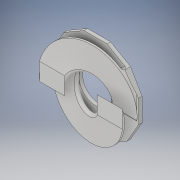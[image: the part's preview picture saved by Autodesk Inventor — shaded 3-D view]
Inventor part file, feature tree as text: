
AUTODESK INVENTOR PART (.ipt)
format: ipt  version: 2018 (Build 220112000, 112)  size: 382,464 bytes
history: native  units: in
note: dims shown in document units (in); Inventor stores cm internally (conversion verified against a paired STEP export)
features: fillet x2, extrude x1, helix x1, sketch x1
ambient origin geometry x8: Origin, YZ Plane, XZ Plane, XY Plane, X Axis, Y Axis, Z Axis, Center Point
bodies: Solid1 (feature_tree)
feature tree (5):
  extrude  "Extrusion1"  Depth=0.125in TaperAngle=0.0deg
  helix  "Coil1"  [1 undecoded]
  fillet  "Fillet1"  Radius=0.3in
  fillet  "Fillet2"  Radius=0.3in
  sketch  "Sketch2"  dims[d0=1.125in d2=0.125in d3=0.0in d4=2.95in d5=0.3in d6=0.3in d7=0.3in d8=0.3in d9=1.0in d10=0.5in d11=0.1969in d12=0.0in d13=90.0deg d14=90.0deg d15=0.0in d16=0.0in d17=0.125in d18=0.05in d19=0.05in d20=0.05in]
note: 1 required parameter value undecoded (feature->parameter linkage not recoverable at this tier; creation-order binding heuristic only, values carry confidence <= 0.55)
